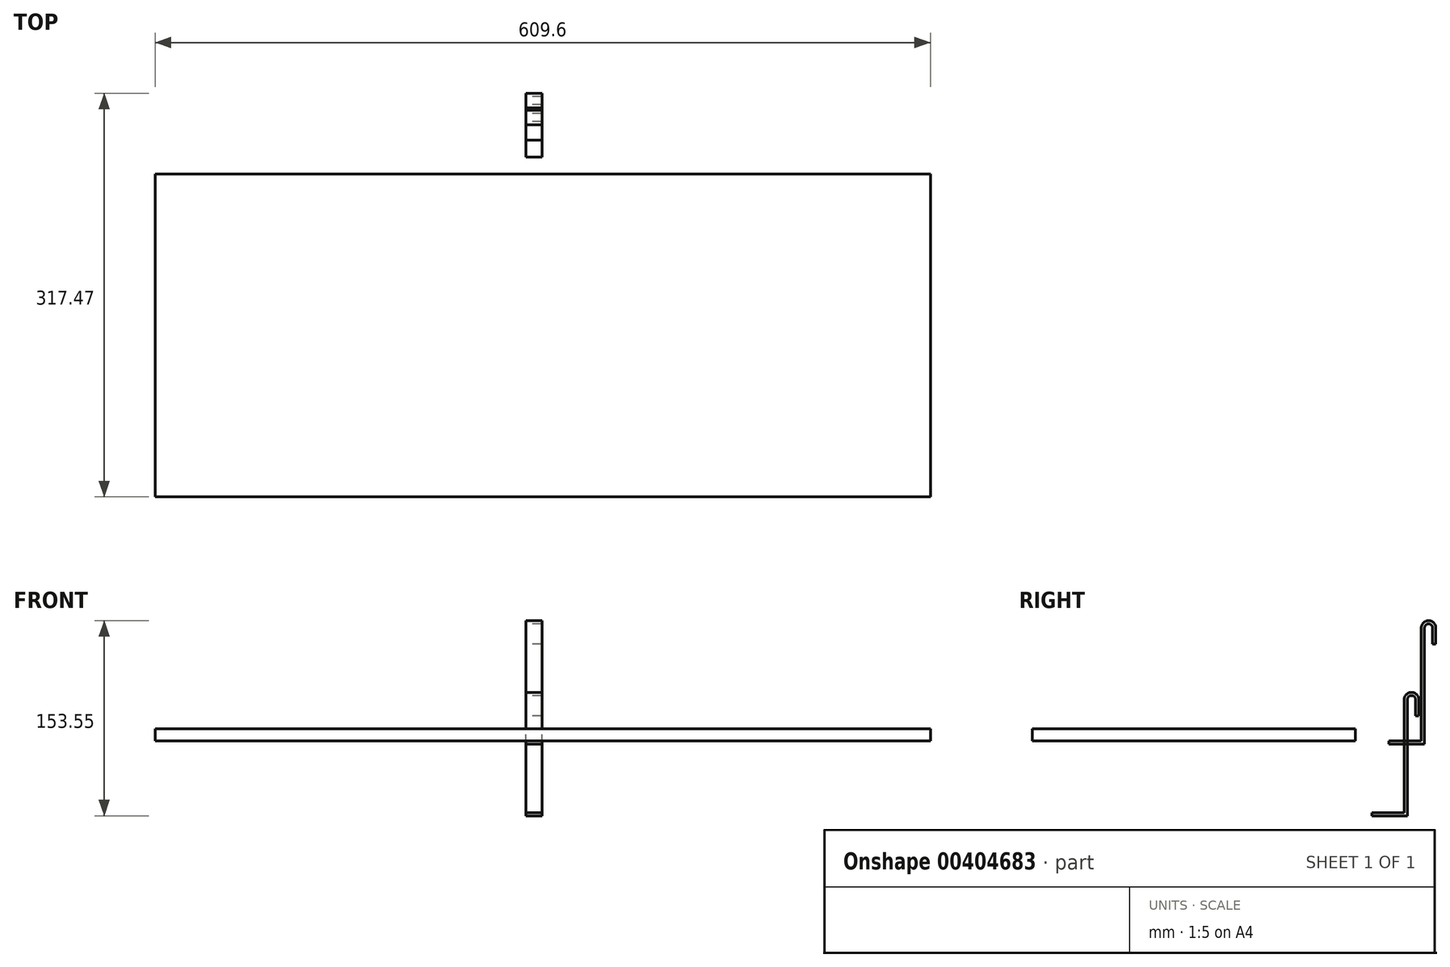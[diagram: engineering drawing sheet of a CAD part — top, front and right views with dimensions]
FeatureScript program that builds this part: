
annotation { "Feature Type Name" : "Feature", "Feature Type Description" : "" }
export const myFeature = defineFeature(function(context is Context, id is Id, definition is map)
    precondition{}
    {
        {
            var Q0;
            Q0=qCreatedBy(makeId("Top.planeOp"),FACE);
            var sketch = newSketch(context, id + "F0", { "sketchPlane" : qUnion([Q0])});
            skLineSegment(sketch, "E0.bottom", {"start": v(-291.5, -169.33) * mm, "end": v(318.1, -169.33) * mm});
            skLineSegment(sketch, "E0.top", {"start": v(-291.5, 84.67) * mm, "end": v(318.1, 84.67) * mm});
            skLineSegment(sketch, "E0.left", {"start": v(-291.5, -169.33) * mm, "end": v(-291.5, 84.67) * mm});
            skLineSegment(sketch, "E0.right", {"start": v(318.1, -169.33) * mm, "end": v(318.1, 84.67) * mm});
            skSolve(sketch);
        }
        {
            var Q0;
            Q0=makeQuery(id+"F0.imprint","IMPRINT",FACE,{"disambiguationData":[TD([[makeQuery(id+"F0.imprint","IMPRINT",EDGE,{"derivedFrom":sQuery(id+"F0.wireOp",EDGE,"E0.bottom")}),1.0]])]});
            extrude(context, id + "F1", {"entities" : qUnion([Q0]), "depth" : 9.52 * mm});
        }
        {
            var Q0;
            Q0=qCreatedBy(makeId("Right.planeOp"),FACE);
            var sketch = newSketch(context, id + "F2", { "sketchPlane" : qUnion([Q0])});
            skLineSegment(sketch, "E1", {"start": v(111.3, 0) * mm, "end": v(136.7, 0) * mm});
            skLineSegment(sketch, "E2", {"start": v(136.7, 0) * mm, "end": v(136.7, 88.9) * mm});
            skArc(sketch, "E3", {"start": v(136.7, 88.9) * mm, "mid": v(142.42, 94.61) * mm, "end": v(148.14, 88.9) * mm});
            skLineSegment(sketch, "E4", {"start": v(148.14, 88.9) * mm, "end": v(148.14, 76.2) * mm});
            skLineSegment(sketch, "E5.0", {"start": v(145.6, 88.9) * mm, "end": v(145.6, 76.2) * mm});
            skArc(sketch, "E5.1", {"start": v(139.25, 88.9) * mm, "mid": v(142.42, 92.08) * mm, "end": v(145.6, 88.9) * mm});
            skLineSegment(sketch, "E5.2", {"start": v(139.25, -2.54) * mm, "end": v(139.25, 88.9) * mm});
            skLineSegment(sketch, "E5.3", {"start": v(111.3, -2.54) * mm, "end": v(139.25, -2.54) * mm});
            skLineSegment(sketch, "E6", {"start": v(145.6, 76.2) * mm, "end": v(148.14, 76.2) * mm});
            skLineSegment(sketch, "E7", {"start": v(111.3, 0) * mm, "end": v(111.3, -2.54) * mm});
            skSolve(sketch);
        }
        {
            var Q0;
            Q0 = qSketchRegion(id + "F2", true);
            extrude(context, id + "F3", {"entities" : qUnion([Q0]), "depth" : 12.7 * mm});
        }
        {
            var Q0;
            Q0=makeQuery(id+"F3.opExtrude","SWEPT_BODY",BODY,{"disambiguationData":[OSD([sQuery(id+"F2.wireOp",EDGE,"E1"),sQuery(id+"F2.wireOp",EDGE,"E2"),sQuery(id+"F2.wireOp",EDGE,"E3"),sQuery(id+"F2.wireOp",EDGE,"E4"),sQuery(id+"F2.wireOp",EDGE,"E5.0"),sQuery(id+"F2.wireOp",EDGE,"E5.1"),sQuery(id+"F2.wireOp",EDGE,"E5.2"),sQuery(id+"F2.wireOp",EDGE,"E5.3"),sQuery(id+"F2.wireOp",EDGE,"E6"),sQuery(id+"F2.wireOp",EDGE,"E7")])]});
            transform(context, id + "F4", {"entities" : qUnion([Q0]), "transformType" : TransformType.TRANSLATION_3D, "dx" : 0 * mm, "dy" : -13.46 * mm, "dz" : -56.4 * mm, "makeCopy" : true});
        }
    });
